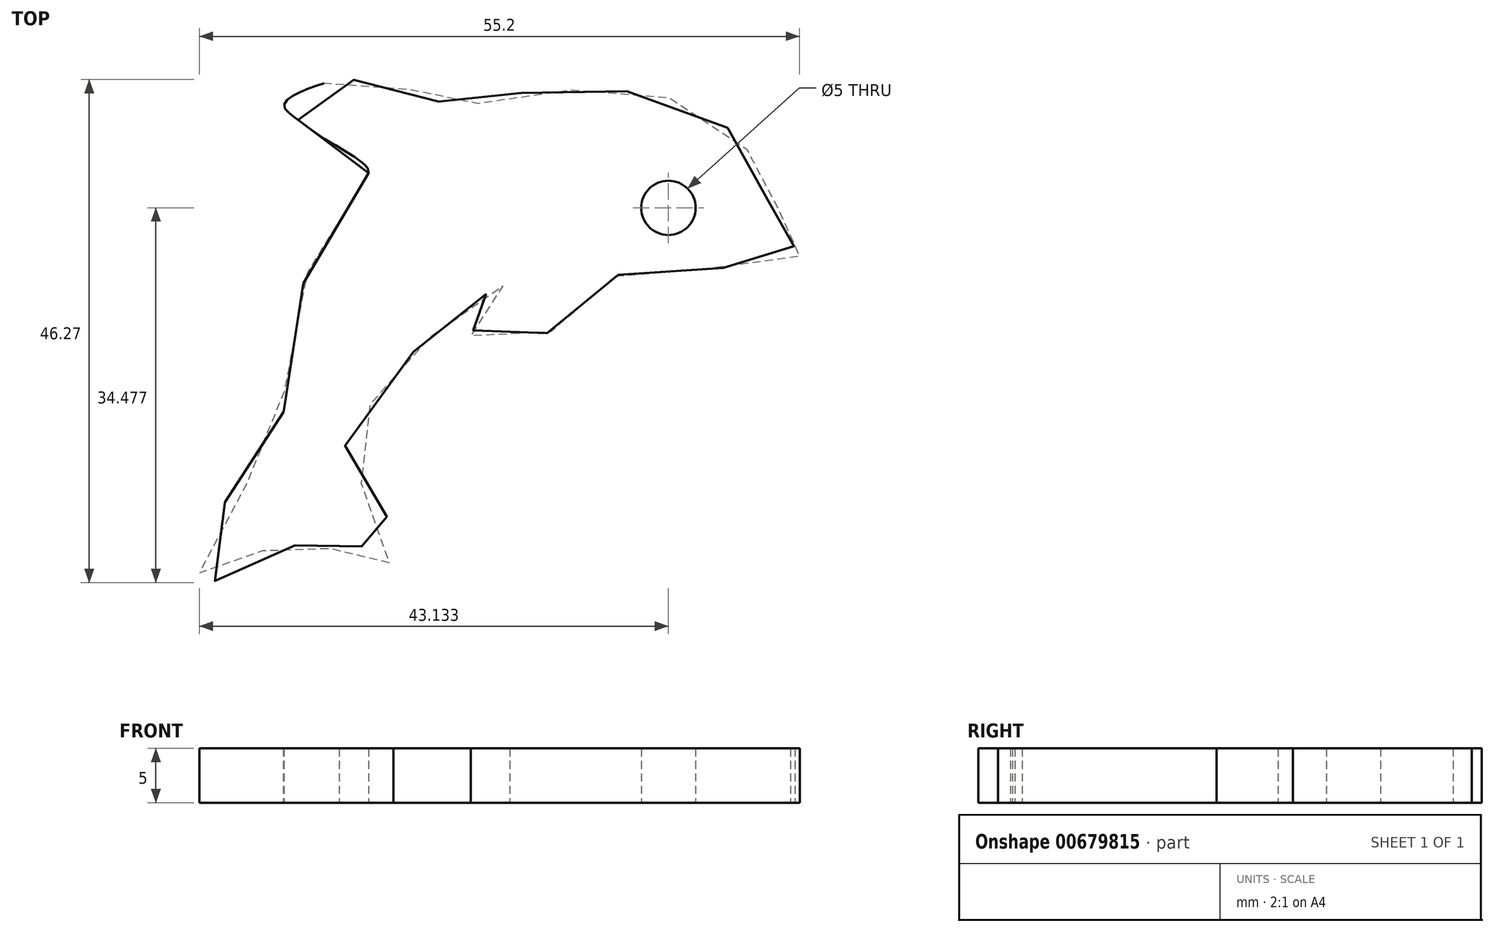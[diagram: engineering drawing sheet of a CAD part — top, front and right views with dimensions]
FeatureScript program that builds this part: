
annotation { "Feature Type Name" : "Feature", "Feature Type Description" : "" }
export const myFeature = defineFeature(function(context is Context, id is Id, definition is map)
    precondition{}
    {
        {
            var Q0;
            Q0=qCreatedBy(makeId("Top.planeOp"),FACE);
            var sketch = newSketch(context, id + "F0", { "sketchPlane" : qUnion([Q0])});
            skFitSpline(sketch, "E0", {"points": [v(-9.48, 15.24) * mm, v(-12.24, 11.8) * mm, v(-14.27, 8.1) * mm, v(-16.1, 3.04) * mm, v(-17, -2.3) * mm, v(-17.23, -5.02) * mm, v(-17.29, -9.87) * mm, v(-17.55, -11.03) * mm, v(-21.32, -13.77) * mm, v(-23.7, -16.56) * mm, v(-24.84, -19.76) * mm, v(-24.84, -22.03) * mm, v(-23.8, -22.4) * mm, v(-22.25, -20.79) * mm, v(-20.6, -19.6) * mm, v(-17.6, -19.5) * mm, v(-16.16, -18.93) * mm, v(-15.64, -18.41) * mm, v(-14.3, -19.19) * mm, v(-12.28, -19.19) * mm, v(-10.89, -19.14) * mm, v(-9.9, -19.14) * mm, v(-8.51, -20.02) * mm, v(-7.69, -20.63) * mm, v(-7.27, -20.12) * mm, v(-7.43, -17.43) * mm, v(-8.62, -15) * mm, v(-10.68, -12.84) * mm, v(-12.02, -11.75) * mm, v(-12.1, -10.89) * mm, v(-9.62, -6.52) * mm, v(-7.57, -3.7) * mm, v(-5.83, -1.68) * mm, v(-4.44, -0.4) * mm, v(-3.05, 0.83) * mm, v(-2.12, 1.6) * mm, v(0.58, 3.65) * mm, v(3.17, 5) * mm, v(3.53, 5.1) * mm, v(2.55, 3.8) * mm, v(0.64, 1.43) * mm, v(0, 0.45) * mm, v(0, 0) * mm, v(1.26, -0.53) * mm, v(3.27, -0.38) * mm, v(6.94, 0.5) * mm, v(9.52, 2.15) * mm, v(11.07, 3.75) * mm, v(12.36, 5.2) * mm, v(14, 6.03) * mm, v(15.97, 6.23) * mm, v(17.93, 6.28) * mm, v(22.58, 6.5) * mm, v(26.3, 6.5) * mm, v(28.78, 6.8) * mm, v(30.16, 7.58) * mm, v(29.7, 8.45) * mm, v(29.34, 8.76) * mm, v(29.65, 9.49) * mm, v(29.65, 10.31) * mm, v(28.72, 11.4) * mm, v(27.64, 12.48) * mm, v(27.23, 12.8) * mm, v(27.02, 14.4) * mm, v(26.25, 16) * mm, v(25.21, 17.6) * mm, v(23.87, 19.14) * mm, v(20.88, 21.1) * mm, v(18.04, 22.19) * mm, v(15.2, 22.65) * mm, v(12.05, 22.91) * mm, v(8.9, 22.86) * mm, v(6, 22.76) * mm, v(3.22, 22.4) * mm, v(0.53, 21.62) * mm, v(-0.86, 21.2) * mm, v(-2.15, 21.41) * mm, v(-3.65, 22.14) * mm, v(-5.5, 22.86) * mm, v(-7.52, 23.48) * mm, v(-9.59, 23.79) * mm, v(-12.27, 23.74) * mm, v(-15.27, 22.91) * mm, v(-17.23, 21.52) * mm, v(-16.14, 20.28) * mm, v(-13.98, 18.68) * mm, v(-12.07, 17.54) * mm, v(-10.05, 16.2) * mm, v(-9.48, 15.24) * mm]});
            skCircle(sketch, "E1", {"center": v(18.1, 12.04) * mm, "radius": 2.5 * mm});
            skSolve(sketch);
        }
        {
            var Q0;
            Q0=makeQuery(id+"F0.imprint","IMPRINT",FACE,{"disambiguationData":[TD([[makeQuery(id+"F0.imprint","IMPRINT",EDGE,{"derivedFrom":sQuery(id+"F0.wireOp",EDGE,"E0")}),1.0]])]});
            extrude(context, id + "F1", {"entities" : qUnion([Q0]), "depth" : 5 * mm, "offsetDistance" : 25 * mm});
        }
    });
